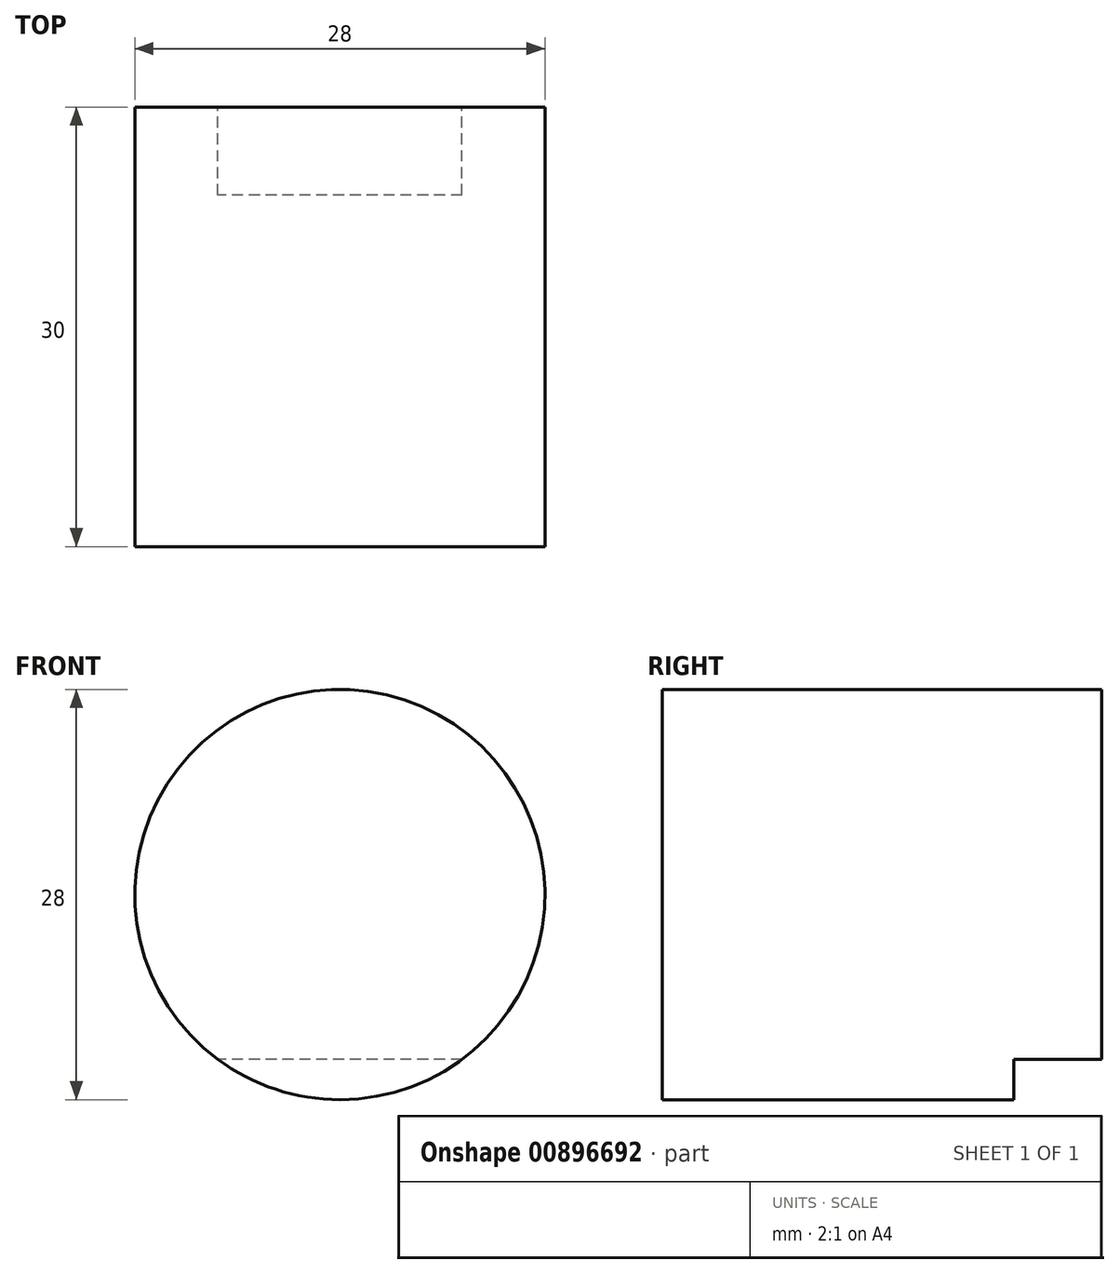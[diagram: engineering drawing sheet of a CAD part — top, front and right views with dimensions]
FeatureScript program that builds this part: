
annotation { "Feature Type Name" : "Feature", "Feature Type Description" : "" }
export const myFeature = defineFeature(function(context is Context, id is Id, definition is map)
    precondition{}
    {
        {
            var Q0;
            Q0=qCreatedBy(makeId("Top.planeOp"),FACE);
            var sketch = newSketch(context, id + "F0", { "sketchPlane" : qUnion([Q0])});
            skLineSegment(sketch, "E0.bottom", {"start": v(27.5, 15) * mm, "end": v(-27.5, 15) * mm});
            skLineSegment(sketch, "E0.top", {"start": v(27.5, -15) * mm, "end": v(-27.5, -15) * mm});
            skLineSegment(sketch, "E0.left", {"start": v(27.5, 15) * mm, "end": v(27.5, -15) * mm});
            skLineSegment(sketch, "E0.right", {"start": v(-27.5, 15) * mm, "end": v(-27.5, -15) * mm});
            skPoint(sketch, "E0.middle", {"position": v(0, 0) * mm});
            skSolve(sketch);
        }
        {
            var Q0;
            Q0 = qSketchRegion(id + "F0", true);
            extrude(context, id + "F1", {"entities" : qUnion([Q0]), "depth" : 117 * mm, "offsetDistance" : 25.4 * mm});
        }
        {
            var Q0;
            Q0=makeQuery(id+"F1.opExtrude","SWEPT_FACE",FACE,{"disambiguationData":[OSD([sQuery(id+"F0.wireOp",EDGE,"E0.bottom")])]});
            var sketch = newSketch(context, id + "F2", { "sketchPlane" : qUnion([Q0])});
            skLineSegment(sketch, "E1", {"start": v(0, 0) * mm, "end": v(0, 117) * mm});
            skLineSegment(sketch, "E2", {"start": v(0, 117) * mm, "end": v(0, 89) * mm});
            skLineSegment(sketch, "E3", {"start": v(0, 0) * mm, "end": v(0, 11) * mm});
            skCircle(sketch, "E4", {"center": v(0, 89) * mm, "radius": 14 * mm});
            skCircle(sketch, "E5", {"center": v(0, 11) * mm, "radius": 4.25 * mm});
            skLineSegment(sketch, "E6.bottom", {"start": v(21.5, 110.5) * mm, "end": v(-21.5, 110.5) * mm});
            skLineSegment(sketch, "E6.top", {"start": v(21.5, 67.5) * mm, "end": v(-21.5, 67.5) * mm});
            skLineSegment(sketch, "E6.left", {"start": v(21.5, 110.5) * mm, "end": v(21.5, 67.5) * mm});
            skLineSegment(sketch, "E6.right", {"start": v(-21.5, 110.5) * mm, "end": v(-21.5, 67.5) * mm});
            skSolve(sketch);
        }
        {
            var Q0;
            Q0 = qSketchRegion(id + "F2", true);
            var Q1;
            {var subQ0=sQuery(id+"F2.wireOp",EDGE,"E2");var subQ1=sQuery(id+"F2.wireOp",EDGE,"E1");var subQ2=makeQuery(id+"F2.imprint","INTERSECT",VERTEX,{"derivedFrom":[subQ1,subQ0]});Q1=makeQuery(id+"F2.imprint","IMPRINT",FACE,{"disambiguationData":[TD([[makeQuery(id+"F2.imprint","IMPRINT",EDGE,{"disambiguationData":[TD([[subQ2,1.0]])],"derivedFrom":subQ1}),1.0]])]});}
            var Q2;
            {var subQ0=sQuery(id+"F2.wireOp",EDGE,"E2");var subQ1=sQuery(id+"F2.wireOp",EDGE,"E1");var subQ2=makeQuery(id+"F2.imprint","INTERSECT",VERTEX,{"derivedFrom":[subQ1,subQ0]});Q2=makeQuery(id+"F2.imprint","IMPRINT",FACE,{"disambiguationData":[TD([[makeQuery(id+"F2.imprint","IMPRINT",EDGE,{"disambiguationData":[TD([[subQ2,1.0]])],"derivedFrom":subQ1}),-1.0]])]});}
            extrude(context, id + "F3", {"entities" : qUnion([Q0, Q1, Q2]), "operationType" : NewBodyOperationType.REMOVE, "oppositeDirection" : true, "depth" : 47.24 * mm, "offsetDistance" : 25.4 * mm});
        }
        {
            var Q0;
            Q0=makeQuery(id+"F1.opExtrude","SWEPT_FACE",FACE,{"disambiguationData":[OSD([sQuery(id+"F0.wireOp",EDGE,"E0.bottom")])]});
            var sketch = newSketch(context, id + "F4", { "sketchPlane" : qUnion([Q0])});
            skLineSegment(sketch, "E7.bottom", {"start": v(-27.5, 77.75) * mm, "end": v(27.5, 77.75) * mm});
            skLineSegment(sketch, "E7.top", {"start": v(-27.5, 25.25) * mm, "end": v(27.5, 25.25) * mm});
            skLineSegment(sketch, "E7.left", {"start": v(-27.5, 77.75) * mm, "end": v(-27.5, 25.25) * mm});
            skLineSegment(sketch, "E7.right", {"start": v(27.5, 77.75) * mm, "end": v(27.5, 25.25) * mm});
            skSolve(sketch);
        }
        {
            var Q0;
            Q0 = qSketchRegion(id + "F4", true);
            extrude(context, id + "F5", {"entities" : qUnion([Q0]), "operationType" : NewBodyOperationType.REMOVE, "oppositeDirection" : true, "depth" : 6 * mm, "offsetDistance" : 25.4 * mm});
        }
    });
